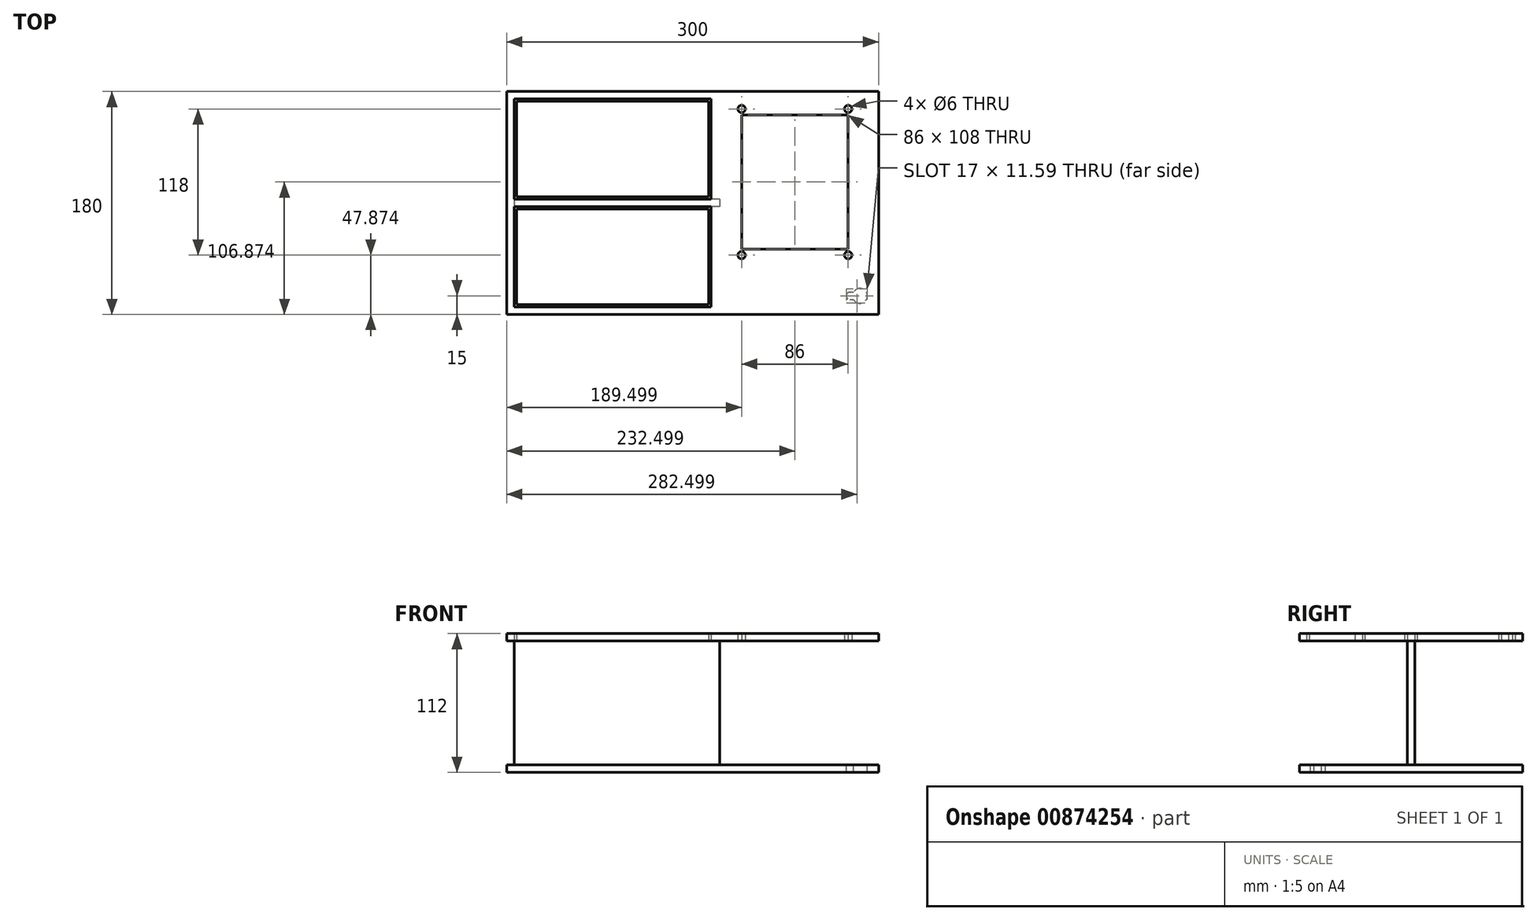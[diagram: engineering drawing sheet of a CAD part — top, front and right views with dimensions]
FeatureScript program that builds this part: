
annotation { "Feature Type Name" : "Feature", "Feature Type Description" : "" }
export const myFeature = defineFeature(function(context is Context, id is Id, definition is map)
    precondition{}
    {
        {
            var Q0;
            Q0=qCreatedBy(makeId("Top.planeOp"),FACE);
            var sketch = newSketch(context, id + "F0", { "sketchPlane" : qUnion([Q0])});
            skCircle(sketch, "E0", {"center": v(-73.66, 75.87) * mm, "radius": 3 * mm});
            skCircle(sketch, "E1", {"center": v(-73.66, -42.13) * mm, "radius": 3 * mm});
            skCircle(sketch, "E2", {"center": v(-159.66, -42.13) * mm, "radius": 3 * mm});
            skCircle(sketch, "E3", {"center": v(-159.66, 75.87) * mm, "radius": 3 * mm});
            skLineSegment(sketch, "E4.bottom", {"start": v(-73.66, 70.87) * mm, "end": v(-159.66, 70.87) * mm});
            skLineSegment(sketch, "E4.top", {"start": v(-73.66, -37.13) * mm, "end": v(-159.66, -37.13) * mm});
            skLineSegment(sketch, "E4.left", {"start": v(-73.66, 70.87) * mm, "end": v(-73.66, -37.13) * mm});
            skLineSegment(sketch, "E4.right", {"start": v(-159.66, 70.87) * mm, "end": v(-159.66, -37.13) * mm});
            skPoint(sketch, "E4.middle", {"position": v(-116.66, 16.87) * mm});
            skLineSegment(sketch, "E5.bottom", {"start": v(-184.16, 3) * mm, "end": v(-343.16, 3) * mm});
            skLineSegment(sketch, "E5.top", {"start": v(-184.16, 84) * mm, "end": v(-343.16, 84) * mm});
            skLineSegment(sketch, "E5.left", {"start": v(-184.16, 3) * mm, "end": v(-184.16, 84) * mm});
            skLineSegment(sketch, "E5.right", {"start": v(-343.16, 3) * mm, "end": v(-343.16, 84) * mm});
            skLineSegment(sketch, "E6.MirrorCS", {"start": v(-343.16, -3) * mm, "end": v(-343.16, -84) * mm});
            skLineSegment(sketch, "E7.MirrorCS", {"start": v(-184.16, -84) * mm, "end": v(-343.16, -84) * mm});
            skLineSegment(sketch, "E8.MirrorCS", {"start": v(-184.16, -3) * mm, "end": v(-343.16, -3) * mm});
            skLineSegment(sketch, "E9.MirrorCS", {"start": v(-184.16, -3) * mm, "end": v(-184.16, -84) * mm});
            skLineSegment(sketch, "E10.bottom", {"start": v(-349.16, 90) * mm, "end": v(-49.16, 90) * mm});
            skLineSegment(sketch, "E10.top", {"start": v(-349.16, -90) * mm, "end": v(-49.16, -90) * mm});
            skLineSegment(sketch, "E10.left", {"start": v(-349.16, 90) * mm, "end": v(-349.16, -90) * mm});
            skLineSegment(sketch, "E10.right", {"start": v(-49.16, 90) * mm, "end": v(-49.16, -90) * mm});
            skLineSegment(sketch, "E11.0", {"start": v(-186.16, 82) * mm, "end": v(-341.16, 82) * mm});
            skLineSegment(sketch, "E11.1", {"start": v(-186.16, 5) * mm, "end": v(-186.16, 82) * mm});
            skLineSegment(sketch, "E11.2", {"start": v(-186.16, 5) * mm, "end": v(-341.16, 5) * mm});
            skLineSegment(sketch, "E11.3", {"start": v(-341.16, 5) * mm, "end": v(-341.16, 82) * mm});
            skLineSegment(sketch, "E12.0", {"start": v(-341.16, -5) * mm, "end": v(-341.16, -82) * mm});
            skLineSegment(sketch, "E12.1", {"start": v(-186.16, -5) * mm, "end": v(-341.16, -5) * mm});
            skLineSegment(sketch, "E12.2", {"start": v(-186.16, -5) * mm, "end": v(-186.16, -82) * mm});
            skLineSegment(sketch, "E12.3", {"start": v(-186.16, -82) * mm, "end": v(-341.16, -82) * mm});
            skSolve(sketch);
        }
        {
            var Q0;
            Q0=makeQuery(id+"F0.imprint","IMPRINT",FACE,{"disambiguationData":[TD([[makeQuery(id+"F0.imprint","IMPRINT",EDGE,{"derivedFrom":sQuery(id+"F0.wireOp",EDGE,"E11.0")}),1.0]])]});
            var Q1;
            Q1=makeQuery(id+"F0.imprint","IMPRINT",FACE,{"disambiguationData":[TD([[makeQuery(id+"F0.imprint","IMPRINT",EDGE,{"derivedFrom":sQuery(id+"F0.wireOp",EDGE,"E12.0")}),1.0]])]});
            var Q2;
            Q2=makeQuery(id+"F0.imprint","IMPRINT",FACE,{"disambiguationData":[TD([[makeQuery(id+"F0.imprint","IMPRINT",EDGE,{"derivedFrom":sQuery(id+"F0.wireOp",EDGE,"E0")}),-1.0]])]});
            extrude(context, id + "F1", {"entities" : qUnion([Q0, Q1, Q2]), "depth" : 6 * mm, "offsetDistance" : 25 * mm});
        }
        {
            var Q0;
            Q0=makeQuery(id+"F1.opExtrude","CAP_FACE",FACE,{"disambiguationData":[OSD([sQuery(id+"F0.wireOp",EDGE,"E0"),sQuery(id+"F0.wireOp",EDGE,"E1"),sQuery(id+"F0.wireOp",EDGE,"E2"),sQuery(id+"F0.wireOp",EDGE,"E3"),sQuery(id+"F0.wireOp",EDGE,"E4.bottom"),sQuery(id+"F0.wireOp",EDGE,"E4.top"),sQuery(id+"F0.wireOp",EDGE,"E4.left"),sQuery(id+"F0.wireOp",EDGE,"E4.right"),sQuery(id+"F0.wireOp",EDGE,"E5.bottom"),sQuery(id+"F0.wireOp",EDGE,"E5.top"),sQuery(id+"F0.wireOp",EDGE,"E5.left"),sQuery(id+"F0.wireOp",EDGE,"E5.right"),sQuery(id+"F0.wireOp",EDGE,"E6.MirrorCS"),sQuery(id+"F0.wireOp",EDGE,"E7.MirrorCS"),sQuery(id+"F0.wireOp",EDGE,"E8.MirrorCS"),sQuery(id+"F0.wireOp",EDGE,"E9.MirrorCS"),sQuery(id+"F0.wireOp",EDGE,"E10.bottom"),sQuery(id+"F0.wireOp",EDGE,"E10.top"),sQuery(id+"F0.wireOp",EDGE,"E10.left"),sQuery(id+"F0.wireOp",EDGE,"E10.right")])],"isStart":true});
            var Q1;
            Q1=makeQuery(id+"F1.opExtrude","CAP_FACE",FACE,{"disambiguationData":[OSD([sQuery(id+"F0.wireOp",EDGE,"E0"),sQuery(id+"F0.wireOp",EDGE,"E1"),sQuery(id+"F0.wireOp",EDGE,"E2"),sQuery(id+"F0.wireOp",EDGE,"E3"),sQuery(id+"F0.wireOp",EDGE,"E4.bottom"),sQuery(id+"F0.wireOp",EDGE,"E4.top"),sQuery(id+"F0.wireOp",EDGE,"E4.left"),sQuery(id+"F0.wireOp",EDGE,"E4.right"),sQuery(id+"F0.wireOp",EDGE,"E5.bottom"),sQuery(id+"F0.wireOp",EDGE,"E5.top"),sQuery(id+"F0.wireOp",EDGE,"E5.left"),sQuery(id+"F0.wireOp",EDGE,"E5.right"),sQuery(id+"F0.wireOp",EDGE,"E6.MirrorCS"),sQuery(id+"F0.wireOp",EDGE,"E7.MirrorCS"),sQuery(id+"F0.wireOp",EDGE,"E8.MirrorCS"),sQuery(id+"F0.wireOp",EDGE,"E9.MirrorCS"),sQuery(id+"F0.wireOp",EDGE,"E10.bottom"),sQuery(id+"F0.wireOp",EDGE,"E10.top"),sQuery(id+"F0.wireOp",EDGE,"E10.left"),sQuery(id+"F0.wireOp",EDGE,"E10.right")])],"isStart":true});
            var Q2;
            Q2=makeQuery(id+"F1.opExtrude","CAP_FACE",FACE,{"disambiguationData":[OSD([sQuery(id+"F0.wireOp",EDGE,"E0"),sQuery(id+"F0.wireOp",EDGE,"E1"),sQuery(id+"F0.wireOp",EDGE,"E2"),sQuery(id+"F0.wireOp",EDGE,"E3"),sQuery(id+"F0.wireOp",EDGE,"E4.bottom"),sQuery(id+"F0.wireOp",EDGE,"E4.top"),sQuery(id+"F0.wireOp",EDGE,"E4.left"),sQuery(id+"F0.wireOp",EDGE,"E4.right"),sQuery(id+"F0.wireOp",EDGE,"E5.bottom"),sQuery(id+"F0.wireOp",EDGE,"E5.top"),sQuery(id+"F0.wireOp",EDGE,"E5.left"),sQuery(id+"F0.wireOp",EDGE,"E5.right"),sQuery(id+"F0.wireOp",EDGE,"E6.MirrorCS"),sQuery(id+"F0.wireOp",EDGE,"E7.MirrorCS"),sQuery(id+"F0.wireOp",EDGE,"E8.MirrorCS"),sQuery(id+"F0.wireOp",EDGE,"E9.MirrorCS"),sQuery(id+"F0.wireOp",EDGE,"E10.bottom"),sQuery(id+"F0.wireOp",EDGE,"E10.top"),sQuery(id+"F0.wireOp",EDGE,"E10.left"),sQuery(id+"F0.wireOp",EDGE,"E10.right")])],"isStart":true});
            var Q3;
            Q3=makeQuery(id+"F1.opExtrude","CAP_FACE",FACE,{"disambiguationData":[OSD([sQuery(id+"F0.wireOp",EDGE,"E0"),sQuery(id+"F0.wireOp",EDGE,"E1"),sQuery(id+"F0.wireOp",EDGE,"E2"),sQuery(id+"F0.wireOp",EDGE,"E3"),sQuery(id+"F0.wireOp",EDGE,"E4.bottom"),sQuery(id+"F0.wireOp",EDGE,"E4.top"),sQuery(id+"F0.wireOp",EDGE,"E4.left"),sQuery(id+"F0.wireOp",EDGE,"E4.right"),sQuery(id+"F0.wireOp",EDGE,"E5.bottom"),sQuery(id+"F0.wireOp",EDGE,"E5.top"),sQuery(id+"F0.wireOp",EDGE,"E5.left"),sQuery(id+"F0.wireOp",EDGE,"E5.right"),sQuery(id+"F0.wireOp",EDGE,"E6.MirrorCS"),sQuery(id+"F0.wireOp",EDGE,"E7.MirrorCS"),sQuery(id+"F0.wireOp",EDGE,"E8.MirrorCS"),sQuery(id+"F0.wireOp",EDGE,"E9.MirrorCS"),sQuery(id+"F0.wireOp",EDGE,"E10.bottom"),sQuery(id+"F0.wireOp",EDGE,"E10.top"),sQuery(id+"F0.wireOp",EDGE,"E10.left"),sQuery(id+"F0.wireOp",EDGE,"E10.right")])],"isStart":true});
            var Q4;
            Q4=makeQuery(id+"F1.opExtrude","CAP_FACE",FACE,{"disambiguationData":[OSD([sQuery(id+"F0.wireOp",EDGE,"E0"),sQuery(id+"F0.wireOp",EDGE,"E1"),sQuery(id+"F0.wireOp",EDGE,"E2"),sQuery(id+"F0.wireOp",EDGE,"E3"),sQuery(id+"F0.wireOp",EDGE,"E4.bottom"),sQuery(id+"F0.wireOp",EDGE,"E4.top"),sQuery(id+"F0.wireOp",EDGE,"E4.left"),sQuery(id+"F0.wireOp",EDGE,"E4.right"),sQuery(id+"F0.wireOp",EDGE,"E5.bottom"),sQuery(id+"F0.wireOp",EDGE,"E5.top"),sQuery(id+"F0.wireOp",EDGE,"E5.left"),sQuery(id+"F0.wireOp",EDGE,"E5.right"),sQuery(id+"F0.wireOp",EDGE,"E6.MirrorCS"),sQuery(id+"F0.wireOp",EDGE,"E7.MirrorCS"),sQuery(id+"F0.wireOp",EDGE,"E8.MirrorCS"),sQuery(id+"F0.wireOp",EDGE,"E9.MirrorCS"),sQuery(id+"F0.wireOp",EDGE,"E10.bottom"),sQuery(id+"F0.wireOp",EDGE,"E10.top"),sQuery(id+"F0.wireOp",EDGE,"E10.left"),sQuery(id+"F0.wireOp",EDGE,"E10.right")])],"isStart":true});
            var sketch = newSketch(context, id + "F2", { "sketchPlane" : qUnion([Q0, Q1, Q2, Q3, Q4])});
            skLineSegment(sketch, "E13.0", {"start": v(-349.16, 90) * mm, "end": v(-49.16, 90) * mm});
            skLineSegment(sketch, "E13.1", {"start": v(-349.16, -90) * mm, "end": v(-49.16, -90) * mm});
            skLineSegment(sketch, "E14.bottom", {"start": v(-177.16, -3) * mm, "end": v(-343.16, -3) * mm});
            skLineSegment(sketch, "E14.top", {"start": v(-177.16, 3) * mm, "end": v(-343.16, 3) * mm});
            skLineSegment(sketch, "E14.left", {"start": v(-177.16, -3) * mm, "end": v(-177.16, 3) * mm});
            skLineSegment(sketch, "E14.right", {"start": v(-343.16, -3) * mm, "end": v(-343.16, 3) * mm});
            skPoint(sketch, "E14.middle", {"position": v(-260.16, 0) * mm});
            skLineSegment(sketch, "E15.bottom", {"start": v(-49.16, -90) * mm, "end": v(-349.16, -90) * mm});
            skLineSegment(sketch, "E15.top", {"start": v(-49.16, 90) * mm, "end": v(-349.16, 90) * mm});
            skLineSegment(sketch, "E15.left", {"start": v(-49.16, -90) * mm, "end": v(-49.16, 90) * mm});
            skLineSegment(sketch, "E15.right", {"start": v(-349.16, -90) * mm, "end": v(-349.16, 90) * mm});
            skLineSegment(sketch, "E16.0", {"start": v(-55.16, 84) * mm, "end": v(-343.16, 84) * mm});
            skLineSegment(sketch, "E16.1", {"start": v(-55.16, -84) * mm, "end": v(-55.16, 84) * mm});
            skLineSegment(sketch, "E16.2", {"start": v(-55.16, -84) * mm, "end": v(-343.16, -84) * mm});
            skLineSegment(sketch, "E16.3", {"start": v(-343.16, -84) * mm, "end": v(-343.16, 84) * mm});
            skLineSegment(sketch, "E17.bottom", {"start": v(-177.16, -84) * mm, "end": v(-183.16, -84) * mm});
            skLineSegment(sketch, "E17.top", {"start": v(-177.16, 84) * mm, "end": v(-183.16, 84) * mm});
            skLineSegment(sketch, "E17.left", {"start": v(-177.16, -84) * mm, "end": v(-177.16, 84) * mm});
            skLineSegment(sketch, "E17.right", {"start": v(-183.16, -84) * mm, "end": v(-183.16, 84) * mm});
            skSolve(sketch);
        }
        {
            var Q0;
            {var subQ4=sQuery(id+"F2.wireOp",EDGE,"E14.bottom");var subQ8=makeQuery(id+"F2.imprint","INTERSECT",VERTEX,{"derivedFrom":[makeQuery(id+"F1.opExtrude","CAP_EDGE",EDGE,{"disambiguationData":[OSD([sQuery(id+"F0.wireOp",EDGE,"E5.left")])],"isStart":true}),subQ4]});Q0=makeQuery(id+"F2.imprint","IMPRINT",FACE,{"disambiguationData":[TD([[makeQuery(id+"F2.imprint","IMPRINT",EDGE,{"disambiguationData":[TD([[subQ8,1.0]])],"derivedFrom":subQ4}),-1.0]])]});}
            var Q1;
            {var subQ0=sQuery(id+"F2.wireOp",EDGE,"E17.left");var subQ1=sQuery(id+"F2.wireOp",EDGE,"E14.bottom");var subQ2=makeQuery(id+"F2.imprint","INTERSECT",VERTEX,{"derivedFrom":[subQ1,subQ0]});Q1=makeQuery(id+"F2.imprint","IMPRINT",FACE,{"disambiguationData":[TD([[makeQuery(id+"F2.imprint","IMPRINT",EDGE,{"disambiguationData":[TD([[subQ2,-1.0]])],"derivedFrom":subQ1}),-1.0]])]});}
            var Q2;
            {var subQ5=sQuery(id+"F2.wireOp",EDGE,"E17.top");Q2=makeQuery(id+"F2.imprint","IMPRINT",FACE,{"disambiguationData":[TD([[makeQuery(id+"F2.imprint","IMPRINT",EDGE,{"derivedFrom":subQ5}),1.0]])]});}
            var Q3;
            {var subQ5=sQuery(id+"F2.wireOp",EDGE,"E17.bottom");Q3=makeQuery(id+"F2.imprint","IMPRINT",FACE,{"disambiguationData":[TD([[makeQuery(id+"F2.imprint","IMPRINT",EDGE,{"derivedFrom":subQ5}),-1.0]])]});}
            var Q4;
            Q4=makeQuery(id+"F2.imprint","IMPRINT",FACE,{"disambiguationData":[TD([[makeQuery(id+"F2.imprint","IMPRINT",EDGE,{"derivedFrom":sQuery(id+"F2.wireOp",EDGE,"E15.bottom")}),1.0]])]});
            extrude(context, id + "F3", {"entities" : qUnion([Q0, Q1, Q2, Q3, Q4]), "operationType" : NewBodyOperationType.ADD, "depth" : 100 * mm, "offsetDistance" : 25 * mm});
        }
        {
            var Q0;
            Q0=makeQuery(id+"F3.opExtrude","CAP_FACE",FACE,{"disambiguationData":[OSD([sQuery(id+"F2.wireOp",EDGE,"E14.bottom"),sQuery(id+"F2.wireOp",EDGE,"E14.top"),sQuery(id+"F2.wireOp",EDGE,"E15.bottom"),sQuery(id+"F2.wireOp",EDGE,"E15.top"),sQuery(id+"F2.wireOp",EDGE,"E15.left"),sQuery(id+"F2.wireOp",EDGE,"E15.right"),sQuery(id+"F2.wireOp",EDGE,"E16.0"),sQuery(id+"F2.wireOp",EDGE,"E16.1"),sQuery(id+"F2.wireOp",EDGE,"E16.2"),sQuery(id+"F2.wireOp",EDGE,"E16.3"),sQuery(id+"F2.wireOp",EDGE,"E17.left"),sQuery(id+"F2.wireOp",EDGE,"E17.right")])],"isStart":false});
            var Q1;
            Q1=makeQuery(id+"F3.opExtrude","CAP_FACE",FACE,{"disambiguationData":[OSD([sQuery(id+"F2.wireOp",EDGE,"E14.bottom"),sQuery(id+"F2.wireOp",EDGE,"E14.top"),sQuery(id+"F2.wireOp",EDGE,"E15.bottom"),sQuery(id+"F2.wireOp",EDGE,"E15.top"),sQuery(id+"F2.wireOp",EDGE,"E15.left"),sQuery(id+"F2.wireOp",EDGE,"E15.right"),sQuery(id+"F2.wireOp",EDGE,"E16.0"),sQuery(id+"F2.wireOp",EDGE,"E16.1"),sQuery(id+"F2.wireOp",EDGE,"E16.2"),sQuery(id+"F2.wireOp",EDGE,"E16.3"),sQuery(id+"F2.wireOp",EDGE,"E17.left"),sQuery(id+"F2.wireOp",EDGE,"E17.right")])],"isStart":false});
            var Q2;
            Q2=makeQuery(id+"F3.opExtrude","CAP_FACE",FACE,{"disambiguationData":[OSD([sQuery(id+"F2.wireOp",EDGE,"E14.bottom"),sQuery(id+"F2.wireOp",EDGE,"E14.top"),sQuery(id+"F2.wireOp",EDGE,"E15.bottom"),sQuery(id+"F2.wireOp",EDGE,"E15.top"),sQuery(id+"F2.wireOp",EDGE,"E15.left"),sQuery(id+"F2.wireOp",EDGE,"E15.right"),sQuery(id+"F2.wireOp",EDGE,"E16.0"),sQuery(id+"F2.wireOp",EDGE,"E16.1"),sQuery(id+"F2.wireOp",EDGE,"E16.2"),sQuery(id+"F2.wireOp",EDGE,"E16.3"),sQuery(id+"F2.wireOp",EDGE,"E17.left"),sQuery(id+"F2.wireOp",EDGE,"E17.right")])],"isStart":false});
            var Q3;
            Q3=makeQuery(id+"F3.opExtrude","CAP_FACE",FACE,{"disambiguationData":[OSD([sQuery(id+"F2.wireOp",EDGE,"E14.bottom"),sQuery(id+"F2.wireOp",EDGE,"E14.top"),sQuery(id+"F2.wireOp",EDGE,"E15.bottom"),sQuery(id+"F2.wireOp",EDGE,"E15.top"),sQuery(id+"F2.wireOp",EDGE,"E15.left"),sQuery(id+"F2.wireOp",EDGE,"E15.right"),sQuery(id+"F2.wireOp",EDGE,"E16.0"),sQuery(id+"F2.wireOp",EDGE,"E16.1"),sQuery(id+"F2.wireOp",EDGE,"E16.2"),sQuery(id+"F2.wireOp",EDGE,"E16.3"),sQuery(id+"F2.wireOp",EDGE,"E17.left"),sQuery(id+"F2.wireOp",EDGE,"E17.right")])],"isStart":false});
            var Q4;
            Q4=makeQuery(id+"F3.opExtrude","CAP_FACE",FACE,{"disambiguationData":[OSD([sQuery(id+"F2.wireOp",EDGE,"E14.bottom"),sQuery(id+"F2.wireOp",EDGE,"E14.top"),sQuery(id+"F2.wireOp",EDGE,"E15.bottom"),sQuery(id+"F2.wireOp",EDGE,"E15.top"),sQuery(id+"F2.wireOp",EDGE,"E15.left"),sQuery(id+"F2.wireOp",EDGE,"E15.right"),sQuery(id+"F2.wireOp",EDGE,"E16.0"),sQuery(id+"F2.wireOp",EDGE,"E16.1"),sQuery(id+"F2.wireOp",EDGE,"E16.2"),sQuery(id+"F2.wireOp",EDGE,"E16.3"),sQuery(id+"F2.wireOp",EDGE,"E17.left"),sQuery(id+"F2.wireOp",EDGE,"E17.right")])],"isStart":false});
            var sketch = newSketch(context, id + "F4", { "sketchPlane" : qUnion([Q0, Q1, Q2, Q3, Q4])});
            skLineSegment(sketch, "E18.bottom", {"start": v(-349.16, -90) * mm, "end": v(-49.16, -90) * mm});
            skLineSegment(sketch, "E18.top", {"start": v(-349.16, 90) * mm, "end": v(-49.16, 90) * mm});
            skLineSegment(sketch, "E18.left", {"start": v(-349.16, -90) * mm, "end": v(-349.16, 90) * mm});
            skLineSegment(sketch, "E18.right", {"start": v(-49.16, -90) * mm, "end": v(-49.16, 90) * mm});
            skCircle(sketch, "E19", {"center": v(-64.16, 75) * mm, "radius": 6 * mm});
            skLineSegment(sketch, "E20.bottom", {"start": v(-72.16, 78) * mm, "end": v(-65.16, 78) * mm});
            skLineSegment(sketch, "E20.top", {"start": v(-72.16, 72) * mm, "end": v(-65.16, 72) * mm});
            skLineSegment(sketch, "E20.left", {"start": v(-75.16, 75) * mm, "end": v(-75.16, 75) * mm});
            skLineSegment(sketch, "E20.right", {"start": v(-65.16, 78) * mm, "end": v(-65.16, 72) * mm});
            skPoint(sketch, "E20.middle", {"position": v(-70.16, 75) * mm});
            skPoint(sketch, "E21.visualSharp", {"position": v(-75.16, 78) * mm});
            skArc(sketch, "E21.filletArc", {"start": v(-72.16, 78) * mm, "mid": v(-74.28, 77.12) * mm, "end": v(-75.16, 75) * mm});
            skPoint(sketch, "E22.visualSharp", {"position": v(-75.16, 72) * mm});
            skArc(sketch, "E22.filletArc", {"start": v(-75.16, 75) * mm, "mid": v(-74.28, 72.88) * mm, "end": v(-72.16, 72) * mm});
            skSolve(sketch);
        }
        {
            var Q0;
            Q0 = qSketchRegion(id + "F4", true);
            extrude(context, id + "F5", {"entities" : qUnion([Q0]), "operationType" : NewBodyOperationType.ADD, "depth" : 6 * mm, "offsetDistance" : 25 * mm});
        }
    });
